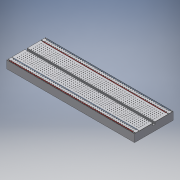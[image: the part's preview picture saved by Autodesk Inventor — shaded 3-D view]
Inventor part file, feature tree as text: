
AUTODESK INVENTOR PART (.ipt)
format: ipt  version: 2017 (Build 210142000, 142)  size: 1,112,576 bytes
history: native  units: mm
features: sketch x5, extrude x4, pattern_circular x2, hole x1, pattern_linear x1, mirror x1, fillet x1
ambient origin geometry x8: Origin, YZ Plane, XZ Plane, XY Plane, X Axis, Y Axis, Z Axis, Center Point
bodies: Solid1 (feature_tree)
feature tree (15):
  extrude  "Extrusion1"  Depth=50.0mm
  extrude  "Extrusion2"  Depth=10.0mm
  extrude  "Extrusion3"  Depth=3.0mm TaperAngle=0.0deg
  pattern_circular  "Circular Pattern1"  Count=16  [1 undecoded]
  hole  "Hole1"  [1 undecoded]
  pattern_linear  "Rectangular Pattern1"  Count1=16 Spacing1=1.0mm
  mirror  "Mirror1"
  pattern_circular  "Circular Pattern2"  Count=2 Angle=360.0deg
  extrude  "Extrusion4"  Depth=2.5mm
  fillet  "Fillet1"  Radius=2.5mm
  sketch  "Sketch1"  dims[d0=165.0mm d1=50.0mm]
  sketch  "Sketch2"  dims[d2=10.0mm d3=0.0mm d4=190.0mm]
  sketch  "Sketch3"  dims[d5=3.0mm d6=3.0mm d7=0.0mm d8=160.0mm]
  sketch  "Sketch4"  dims[d9=1.0mm d10=0.1mm d11=0.0mm d12=160.0mm d13=1.0mm d14=5.0mm d15=20.0mm d16=360.0deg]
  sketch  "Sketch5"  dims[d18=2.5mm d19=2.5mm d20=2.5mm d21=2.5mm d22=2.5mm d26=2.5mm d27=0.7mm d28=6.0mm d29=4.0mm d30=2.0mm d31=90.0deg d32=5.0mm d33=20.594885mm d34=300.0mm d36=2.7mm d37=20.0mm d38=360.0deg d40=0.1mm d41=0.0mm d42=0.2mm]
note: 2 required parameter values undecoded (feature->parameter linkage not recoverable at this tier; creation-order binding heuristic only, values carry confidence <= 0.55)
